# Revit family: d0061921_REVIT-150-250 HST
name_source: partatom
category: Mechanical Equipment
revit_build: Autodesk Revit 2016 (Build: 20150714_1515(x64)
units: mm (PartAtom-declared; Revit-internal decimal feet)

## family parameters
Always vertical = Yes
Cut with Voids When Loaded = No
Part Type = Normal
Room Calculation Point = No
Round Connector Dimension = Use Radius
Shared = No
Work Plane-Based = No

## types (4) — shared parameters
Assembly Code = D3040400
Circulating Inlet Extension = 19 5/32"
Circulating Inlet NPT = 3"
Circulating Inlet Radius = 1 1/2"
Circulating Outlet Extension = 18"
Circulating Outlet NPT = 3"
Circulating Outlet Radius = 1 1/2"
Clearance Front = 67 5/8"
Clearance Rear = 59 1/8"
Cold Inlet Extension = 19 5/32"
Cold Inlet NPT = 2"
Cold Inlet Radius = 1"
Cold Inlet To Rear = 14 1/2"
Disclaimer = This rendering is for building modeling purposes only. Submittal/catalog is still the contract document. PVI reserves the right to change design and specification without notice.
Drain Extension = 21 5/32"
Drain Location = 24"
Drain NPT = 1"
Drain Radius = 1/2"
Flat Side Spacing = 34"
Height to Energy = 24 1/2"
Height to Relief = 45 1/8"
Hot Outlet Extension = 19 5/32"
Hot Outlet NPT = 2"
Hot Outlet Radius = 1"
Lifting Lugs To Rear = 23"
Manufacturer = PVI Industries, LLC
Rear Skid Extension = 22 5/8"
Relief Extension = 19 5/32"
Relief Valve NPT = 1"
Relief Valve Radius = 1/2"
Relief to Rear = 14 1/2"
Skid Center Dist = 9"
Skid Spacing = 18"
Temperature Gauge Fitting NPT = 3/4"
Temperature Gauge Fitting Radius = 3/8"
Thermowell Fitting Extension = 18"
Thermowell Fitting NPT = 3/4"
Thermowell Fitting Radius = 3/8"
URL = www.pvi.com
Unit Radius = 18 5/32"

## per-type parameters (varying)
| type | Circulating Inlet Angle | Description | Front Skid Extension | Hot Outlet To Front | Model | Nominal Storage | Size | Skid Length | Skid To Rear | Thermowell Fitting To Rear | Unit Length | Weight |
| LH 250A-TR | 45.00° | PVI Turbopower - Water Heater | 98 5/8" | 11 1/4" | LH 250A-TR | 250 gal | 250 | 76" | 11 1/8" | 50 3/4" | 94" | 770 |
| LH 175A-TR | 46.13° | PVI AquaPLEX® Storage Tanks - Horizontal Storage Tanks | 72 5/8" | 10 39/64" | LH 175A-TR | 175 gal | 175 | 50" | 12 1/8" | 38 1/4" | 68 1/2" | 710 |
| LH 150A-TR | 46.13° | PVI AquaPLEX® Storage Tanks - Horizontal Storage Tanks | 66 5/8" | 11 1/4" | LH 150A-TR | 150 gal | 150 | 44" | 12 1/8" | 35 1/4" | 62 1/2" | 695 |
| LH 215A-TR | 46.13° | PVI Turbopower - Water Heater | 78 5/8" | 11 1/4" | LH 250A-TR | 215 gal | 215 | 56" | 12 1/8" | 41 1/4" | 75" | 730 |

## geometry (parser evidence)
native form markers: Sweep x3
no freeform markers — native parametric forms only
